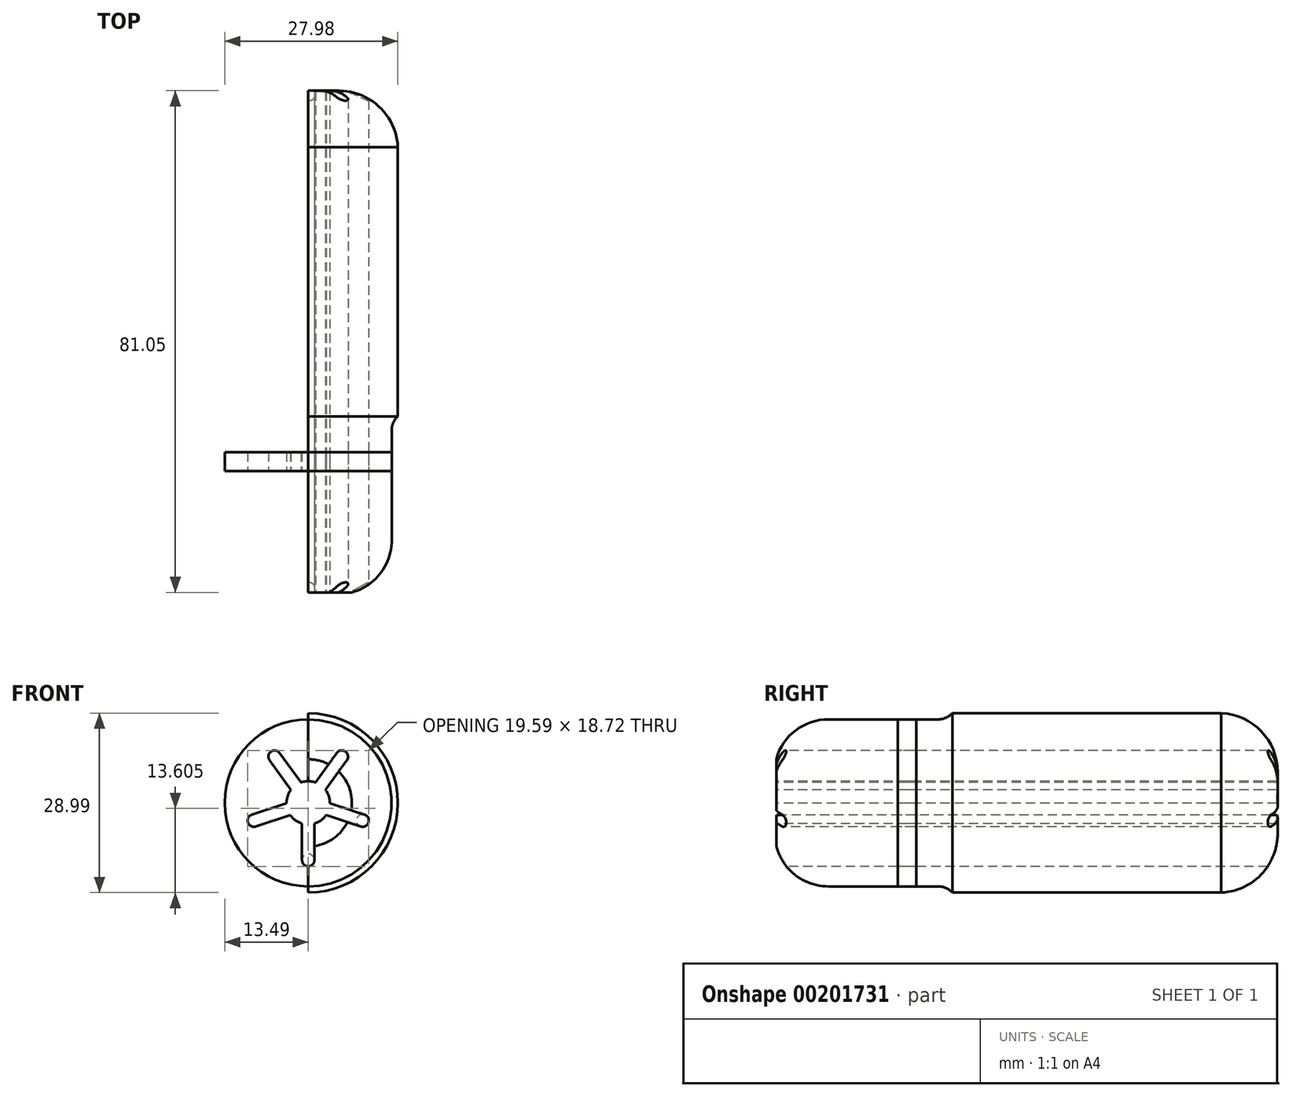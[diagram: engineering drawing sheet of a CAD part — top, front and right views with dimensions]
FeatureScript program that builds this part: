
annotation { "Feature Type Name" : "Feature", "Feature Type Description" : "" }
export const myFeature = defineFeature(function(context is Context, id is Id, definition is map)
    precondition{}
    {
        {
            var Q0;
            Q0=qCreatedBy(makeId("Right.planeOp"),FACE);
            var sketch = newSketch(context, id + "F0", { "sketchPlane" : qUnion([Q0])});
            skLineSegment(sketch, "E0.bottom", {"start": v(-3.13, 33.38) * mm, "end": v(86.87, 33.38) * mm});
            skLineSegment(sketch, "E0.top", {"start": v(-3.13, 32.38) * mm, "end": v(4.08, 32.38) * mm});
            skLineSegment(sketch, "E0.left", {"start": v(-3.13, 33.38) * mm, "end": v(-3.13, 32.38) * mm});
            skLineSegment(sketch, "E0.right", {"start": v(86.87, 33.38) * mm, "end": v(86.87, 32.38) * mm});
            skPoint(sketch, "E0.middle", {"position": v(41.87, 32.88) * mm});
            skLineSegment(sketch, "E1.bottom", {"start": v(86.87, 32.38) * mm, "end": v(81.87, 32.38) * mm, "construction": true});
            skLineSegment(sketch, "E1.top", {"start": v(86.87, 21.38) * mm, "end": v(85.87, 21.38) * mm});
            skLineSegment(sketch, "E1.left", {"start": v(86.87, 32.38) * mm, "end": v(86.87, 21.38) * mm, "construction": true});
            skLineSegment(sketch, "E1.right", {"start": v(81.87, 32.38) * mm, "end": v(81.87, 21.38) * mm, "construction": true});
            skLineSegment(sketch, "E2.bottom", {"start": v(81.87, 32.38) * mm, "end": v(71.87, 32.38) * mm, "construction": true});
            skLineSegment(sketch, "E2.top", {"start": v(81.87, 21.38) * mm, "end": v(71.87, 21.38) * mm, "construction": true});
            skLineSegment(sketch, "E2.right", {"start": v(71.87, 33.38) * mm, "end": v(71.87, 21.38) * mm, "construction": true});
            skLineSegment(sketch, "E3.0", {"start": v(85.87, 22.38) * mm, "end": v(85.37, 22.38) * mm, "construction": true});
            skLineSegment(sketch, "E4.0", {"start": v(85.87, 32.38) * mm, "end": v(85.87, 21.38) * mm, "construction": true});
            skArc(sketch, "E5", {"start": v(82.3, 22.38) * mm, "mid": v(80.84, 28.3) * mm, "end": v(76.33, 32.38) * mm});
            skArc(sketch, "E6", {"start": v(81.87, 21.38) * mm, "mid": v(79.3, 29.1) * mm, "end": v(71.87, 32.38) * mm});
            skLineSegment(sketch, "E7.trimOffspring", {"start": v(76.33, 32.38) * mm, "end": v(86.87, 32.38) * mm});
            skLineSegment(sketch, "E8.top", {"start": v(86.87, 25.38) * mm, "end": v(85.87, 25.38) * mm});
            skLineSegment(sketch, "E8.left", {"start": v(86.87, 23.38) * mm, "end": v(86.87, 25.38) * mm});
            skLineSegment(sketch, "E8.right", {"start": v(85.87, 22.38) * mm, "end": v(85.87, 22.72) * mm, "construction": true});
            skLineSegment(sketch, "E9.bottom", {"start": v(-3.13, 32.38) * mm, "end": v(-2.13, 32.38) * mm, "construction": true});
            skLineSegment(sketch, "E9.top", {"start": v(-3.13, 21.38) * mm, "end": v(-2.13, 21.38) * mm});
            skLineSegment(sketch, "E9.left", {"start": v(-3.13, 32.38) * mm, "end": v(-3.13, 21.38) * mm, "construction": true});
            skLineSegment(sketch, "E9.right", {"start": v(-2.13, 32.38) * mm, "end": v(-2.13, 21.38) * mm, "construction": true});
            skLineSegment(sketch, "E10.bottom", {"start": v(-2.13, 32.38) * mm, "end": v(4.08, 32.38) * mm, "construction": true});
            skLineSegment(sketch, "E10.top", {"start": v(-2.13, 33.38) * mm, "end": v(8.87, 33.38) * mm, "construction": true});
            skLineSegment(sketch, "E10.left", {"start": v(-2.13, 32.38) * mm, "end": v(-2.13, 33.38) * mm, "construction": true});
            skLineSegment(sketch, "E10.right", {"start": v(8.87, 32.38) * mm, "end": v(8.87, 33.38) * mm, "construction": true});
            skArc(sketch, "E11", {"start": v(4.08, 32.38) * mm, "mid": v(-1.17, 27.96) * mm, "end": v(-3.13, 21.38) * mm});
            skArc(sketch, "E12", {"start": v(8.87, 32.38) * mm, "mid": v(1.1, 29.16) * mm, "end": v(-2.13, 21.38) * mm});
            skLineSegment(sketch, "E13.trimOffspring", {"start": v(8.87, 32.38) * mm, "end": v(71.87, 32.38) * mm});
            skLineSegment(sketch, "E14", {"start": v(8.87, 21.38) * mm, "end": v(71.87, 21.38) * mm, "construction": true});
            skLineSegment(sketch, "E15.0", {"start": v(8.87, 17.38) * mm, "end": v(71.87, 17.38) * mm, "construction": true});
            skLineSegment(sketch, "E16.0", {"start": v(86.87, 23.38) * mm, "end": v(85.87, 23.38) * mm, "construction": true});
            skLineSegment(sketch, "E17.0", {"start": v(83.87, 21.38) * mm, "end": v(83.87, 25.38) * mm, "construction": true});
            skLineSegment(sketch, "E18", {"start": v(86.87, 23.38) * mm, "end": v(83.87, 21.38) * mm});
            skLineSegment(sketch, "E19.0", {"start": v(85.87, 23.92) * mm, "end": v(83.57, 22.38) * mm});
            skLineSegment(sketch, "E20.trimOffspring", {"start": v(83.87, 21.38) * mm, "end": v(81.87, 21.38) * mm});
            skLineSegment(sketch, "E21.trimOffspring", {"start": v(83.57, 22.38) * mm, "end": v(82.3, 22.38) * mm});
            skLineSegment(sketch, "E22.trimOffspring", {"start": v(85.87, 23.92) * mm, "end": v(85.87, 25.38) * mm});
            skLineSegment(sketch, "E23.bottom", {"start": v(8.87, 17.38) * mm, "end": v(-3.13, 17.38) * mm, "construction": true});
            skLineSegment(sketch, "E23.top", {"start": v(8.87, 21.38) * mm, "end": v(-3.13, 21.38) * mm, "construction": true});
            skLineSegment(sketch, "E23.left", {"start": v(8.87, 17.38) * mm, "end": v(8.87, 21.38) * mm, "construction": true});
            skLineSegment(sketch, "E23.right", {"start": v(-3.13, 17.38) * mm, "end": v(-3.13, 21.38) * mm, "construction": true});
            skSolve(sketch);
        }
        {
            var Q0;
            Q0=qCreatedBy(makeId("Right.planeOp"),FACE);
            var sketch = newSketch(context, id + "F1", { "sketchPlane" : qUnion([Q0])});
            skLineSegment(sketch, "E24.bottom", {"start": v(-3.13, 33.38) * mm, "end": v(28.58, 33.38) * mm, "construction": true});
            skLineSegment(sketch, "E24.left", {"start": v(-3.13, 33.38) * mm, "end": v(-3.13, 23.38) * mm, "construction": true});
            skLineSegment(sketch, "E24.right", {"start": v(28.58, 33.38) * mm, "end": v(28.58, 33.38) * mm});
            skLineSegment(sketch, "E25", {"start": v(28.58, 32.38) * mm, "end": v(8.84, 32.38) * mm, "construction": true});
            skArc(sketch, "E26", {"start": v(8.84, 32.38) * mm, "mid": v(1.84, 29.83) * mm, "end": v(-1.88, 23.38) * mm, "construction": true});
            skLineSegment(sketch, "E27.0", {"start": v(27.9, 31.88) * mm, "end": v(8.84, 31.88) * mm});
            skArc(sketch, "E28.0", {"start": v(8.84, 31.88) * mm, "mid": v(2.16, 29.45) * mm, "end": v(-1.38, 23.3) * mm});
            skLineSegment(sketch, "E29.0", {"start": v(26.58, 31.38) * mm, "end": v(8.84, 31.38) * mm});
            skArc(sketch, "E30.0", {"start": v(8.84, 30.88) * mm, "mid": v(2.9, 28.77) * mm, "end": v(-0.35, 23.38) * mm, "construction": true});
            skPoint(sketch, "E31.newPointB", {"position": v(28.58, 23.38) * mm});
            skArc(sketch, "E31.filletArc", {"start": v(26.58, 31.38) * mm, "mid": v(27.3, 31.5) * mm, "end": v(27.9, 31.88) * mm});
            skArc(sketch, "E32", {"start": v(8.84, 31.38) * mm, "mid": v(2.64, 29.01) * mm, "end": v(-0.4, 23.12) * mm});
            skLineSegment(sketch, "E33.trimOffspring", {"start": v(-1.37, 23.38) * mm, "end": v(-0.35, 23.38) * mm});
            skSolve(sketch);
        }
        {
            var Q0;
            Q0=qCreatedBy(makeId("Right.planeOp"),FACE);
            var sketch = newSketch(context, id + "F2", { "sketchPlane" : qUnion([Q0])});
            skLineSegment(sketch, "E34", {"start": v(86.87, 23.38) * mm, "end": v(83.87, 21.38) * mm, "construction": true});
            skLineSegment(sketch, "E35", {"start": v(83.87, 21.38) * mm, "end": v(81.87, 21.38) * mm, "construction": true});
            skLineSegment(sketch, "E36.0", {"start": v(86.87, 22.78) * mm, "end": v(84.02, 20.88) * mm});
            skLineSegment(sketch, "E37.0", {"start": v(84.02, 20.88) * mm, "end": v(81.87, 20.88) * mm});
            skLineSegment(sketch, "E38", {"start": v(86.87, 22.78) * mm, "end": v(86.87, 17.38) * mm});
            skLineSegment(sketch, "E39.0", {"start": v(66.87, 20.38) * mm, "end": v(66.87, 17.38) * mm});
            skLineSegment(sketch, "E40.0", {"start": v(81.87, 20.38) * mm, "end": v(66.87, 20.38) * mm});
            skLineSegment(sketch, "E41", {"start": v(71.87, 17.38) * mm, "end": v(66.87, 17.38) * mm});
            skLineSegment(sketch, "E42", {"start": v(71.87, 17.38) * mm, "end": v(86.87, 17.38) * mm});
            skLineSegment(sketch, "E43.0", {"start": v(81.87, 20.88) * mm, "end": v(81.87, 20.38) * mm});
            skSolve(sketch);
        }
        {
            var Q0;
            Q0=qCreatedBy(makeId("Right.planeOp"),FACE);
            var sketch = newSketch(context, id + "F3", { "sketchPlane" : qUnion([Q0])});
            skArc(sketch, "E44", {"start": v(81.87, 21.38) * mm, "mid": v(79.3, 29.1) * mm, "end": v(71.87, 32.38) * mm, "construction": true});
            skArc(sketch, "E45.0", {"start": v(81.3, 20.88) * mm, "mid": v(79.25, 28.4) * mm, "end": v(72.28, 31.88) * mm});
            skLineSegment(sketch, "E46", {"start": v(81.87, 20.38) * mm, "end": v(69.18, 20.38) * mm, "construction": true});
            skLineSegment(sketch, "E47", {"start": v(28.58, 32.38) * mm, "end": v(37.05, 32.38) * mm});
            skLineSegment(sketch, "E48", {"start": v(26.58, 31.38) * mm, "end": v(22.5, 31.38) * mm});
            skArc(sketch, "E49", {"start": v(26.58, 31.38) * mm, "mid": v(27.7, 31.64) * mm, "end": v(28.58, 32.38) * mm});
            skLineSegment(sketch, "E50.0", {"start": v(28.58, 31.88) * mm, "end": v(72.28, 31.88) * mm});
            skArc(sketch, "E51.0", {"start": v(26.58, 30.88) * mm, "mid": v(27.93, 31.2) * mm, "end": v(28.98, 32.08) * mm});
            skLineSegment(sketch, "E52.0", {"start": v(26.58, 30.88) * mm, "end": v(8.74, 30.88) * mm});
            skLineSegment(sketch, "E53.0", {"start": v(81.3, 20.88) * mm, "end": v(0.37, 20.88) * mm});
            skArc(sketch, "E54", {"start": v(8.84, 31.38) * mm, "mid": v(2.74, 29.11) * mm, "end": v(-0.35, 23.38) * mm, "construction": true});
            skArc(sketch, "E55.0", {"start": v(8.83, 30.88) * mm, "mid": v(3.5, 29.1) * mm, "end": v(0.37, 24.44) * mm});
            skLineSegment(sketch, "E56", {"start": v(-2.13, 27.58) * mm, "end": v(-2.13, 15.19) * mm, "construction": true});
            skLineSegment(sketch, "E57.trimOffspring", {"start": v(0.37, 24.44) * mm, "end": v(0.37, 20.88) * mm});
            skSolve(sketch);
        }
        {
            var Q0;
            Q0=qSketchRegion(id+"F3",true);
            var Q1;
            Q1=sQuery(id+"F0.wireOp",EDGE,"E15.0");
            revolve(context, id + "F4", {"entities" : qUnion([Q0]), "axis" : qUnion([Q1]), "revolveType" : RevolveType.ONE_DIRECTION, "angle" : 180 * degree});
        }
        {
            var Q0;
            Q0=qCreatedBy(makeId("Front.planeOp"),FACE);
            var sketch = newSketch(context, id + "F5", { "sketchPlane" : qUnion([Q0])});
            skCircle(sketch, "E58", {"center": v(0, 17.38) * mm, "radius": 14.5 * mm, "construction": true});
            skCircle(sketch, "E59", {"center": v(0, 17.38) * mm, "radius": 3.5 * mm});
            skLineSegment(sketch, "E60", {"start": v(0, 17.38) * mm, "end": v(0, 4.9) * mm, "construction": true});
            skPoint(sketch, "E61", {"position": v(0, 4.9) * mm});
            skPoint(sketch, "E62", {"position": v(-16.26, 26.77) * mm});
            skLineSegment(sketch, "E63.0", {"start": v(-1, 14.03) * mm, "end": v(-1, 8.13) * mm});
            skLineSegment(sketch, "E64.0", {"start": v(1, 14.03) * mm, "end": v(1, 8.13) * mm});
            skLineSegment(sketch, "E65", {"start": v(0, 7.13) * mm, "end": v(0, 7.13) * mm});
            skPoint(sketch, "E66.visualSharp", {"position": v(-1, 7.13) * mm});
            skArc(sketch, "E66.filletArc", {"start": v(-1, 8.13) * mm, "mid": v(-0.7, 7.43) * mm, "end": v(0, 7.13) * mm});
            skPoint(sketch, "E67.visualSharp", {"position": v(1, 7.13) * mm});
            skArc(sketch, "E67.filletArc", {"start": v(0, 7.13) * mm, "mid": v(0.7, 7.43) * mm, "end": v(1, 8.13) * mm});
            skSolve(sketch);
        }
        {
            var Q0;
            {var subQ0=sQuery(id+"F5.wireOp",EDGE,"E63.0");Q0=makeQuery(id+"F5.imprint","IMPRINT",FACE,{"disambiguationData":[TD([[makeQuery(id+"F5.imprint","IMPRINT",EDGE,{"derivedFrom":subQ0}),1.0]])]});}
            extrude(context, id + "F6", {"entities" : qUnion([Q0]), "oppositeDirection" : true, "depth" : 90 * mm});
        }
        {
            var Q0;
            Q0=qCreatedBy(makeId("Right.planeOp"),FACE);
            var sketch = newSketch(context, id + "F7", { "sketchPlane" : qUnion([Q0])});
            skLineSegment(sketch, "E68", {"start": v(0, 17.38) * mm, "end": v(41.07, 17.38) * mm});
            skSolve(sketch);
        }
        {
            var Q0;
            Q0=makeQuery(id+"F6.opExtrude","SWEPT_BODY",BODY,{"disambiguationData":[OSD([sQuery(id+"F5.wireOp",EDGE,"E59"),sQuery(id+"F5.wireOp",EDGE,"E63.0"),sQuery(id+"F5.wireOp",EDGE,"E64.0"),sQuery(id+"F5.wireOp",EDGE,"c18d3147-b101-4655-83fc-4fb6f8fd4f04")])]});
            var Q1;
            Q1=sQuery(id+"F7.wireOp",EDGE,"E68");
            circularPattern(context, id + "F8", {"entities" : qUnion([Q0]), "axis" : qUnion([Q1]), "angle" : 360 * degree, "instanceCount" : 5, "equalSpace" : true});
        }
        {
            var Q0;
            Q0=makeQuery(id+"F6.opExtrude","SWEPT_BODY",BODY,{"disambiguationData":[OSD([sQuery(id+"F5.wireOp",EDGE,"E59"),sQuery(id+"F5.wireOp",EDGE,"E63.0"),sQuery(id+"F5.wireOp",EDGE,"E64.0"),sQuery(id+"F5.wireOp",EDGE,"E66.filletArc"),sQuery(id+"F5.wireOp",EDGE,"E67.filletArc")])]});
            var Q1;
            Q1=makeQuery(id+"F8.opPattern","COPY",BODY,{"derivedFrom":makeQuery(id+"F6.opExtrude","SWEPT_BODY",BODY,{"disambiguationData":[OSD([sQuery(id+"F5.wireOp",EDGE,"E59"),sQuery(id+"F5.wireOp",EDGE,"E63.0"),sQuery(id+"F5.wireOp",EDGE,"E64.0"),sQuery(id+"F5.wireOp",EDGE,"E66.filletArc"),sQuery(id+"F5.wireOp",EDGE,"E67.filletArc")])]}),"instanceName":"4"});
            var Q2;
            Q2=makeQuery(id+"F8.opPattern","COPY",BODY,{"derivedFrom":makeQuery(id+"F6.opExtrude","SWEPT_BODY",BODY,{"disambiguationData":[OSD([sQuery(id+"F5.wireOp",EDGE,"E59"),sQuery(id+"F5.wireOp",EDGE,"E63.0"),sQuery(id+"F5.wireOp",EDGE,"E64.0"),sQuery(id+"F5.wireOp",EDGE,"E66.filletArc"),sQuery(id+"F5.wireOp",EDGE,"E67.filletArc")])]}),"instanceName":"3"});
            var Q3;
            Q3=makeQuery(id+"F4.opRevolve","SWEPT_BODY",BODY,{"disambiguationData":[OSD([sQuery(id+"F3.wireOp",EDGE,"E45.0"),sQuery(id+"F3.wireOp",EDGE,"E50.0"),sQuery(id+"F3.wireOp",EDGE,"E51.0"),sQuery(id+"F3.wireOp",EDGE,"E52.0"),sQuery(id+"F3.wireOp",EDGE,"E53.0"),sQuery(id+"F3.wireOp",EDGE,"E55.0"),sQuery(id+"F3.wireOp",EDGE,"E57.trimOffspring")])]});
            booleanBodies(context, id + "F9", {"operationType" : BooleanOperationType.SUBTRACTION, "tools" : qUnion([Q0, Q1, Q2]), "targets" : qUnion([Q3]), "keepTools" : true});
        }
        {
            var Q0;
            Q0 = qSketchRegion(id + "F3", true);
            var Q1;
            Q1=sQuery(id+"F0.wireOp",EDGE,"E15.0");
            revolve(context, id + "F10", {"entities" : qUnion([Q0]), "axis" : qUnion([Q1]), "revolveType" : RevolveType.FULL});
        }
        {
            var Q0;
            Q0=qCreatedBy(makeId("Front.planeOp"),FACE);
            var sketch = newSketch(context, id + "F11", { "sketchPlane" : qUnion([Q0])});
            skCircle(sketch, "E69.0", {"center": v(0, 17.38) * mm, "radius": 13.5 * mm});
            skSolve(sketch);
        }
        {
            var Q0;
            Q0=makeQuery(id+"F11.imprint","IMPRINT",FACE,{"disambiguationData":[TD([[makeQuery(id+"F11.imprint","IMPRINT",EDGE,{"derivedFrom":sQuery(id+"F11.wireOp",EDGE,"E69.0")}),1.0]])]});
            extrude(context, id + "F12", {"entities" : qUnion([Q0]), "oppositeDirection" : true, "depth" : 23 * mm, "hasSecondDirection" : true, "secondDirectionOppositeDirection" : true, "secondDirectionDepth" : 20 * mm});
        }
        {
            var Q0;
            Q0=makeQuery(id+"F6.opExtrude","SWEPT_BODY",BODY,{"disambiguationData":[OSD([sQuery(id+"F5.wireOp",EDGE,"E59"),sQuery(id+"F5.wireOp",EDGE,"E63.0"),sQuery(id+"F5.wireOp",EDGE,"E64.0"),sQuery(id+"F5.wireOp",EDGE,"E66.filletArc"),sQuery(id+"F5.wireOp",EDGE,"E67.filletArc")])]});
            var Q1;
            Q1=makeQuery(id+"F8.opPattern","COPY",BODY,{"derivedFrom":makeQuery(id+"F6.opExtrude","SWEPT_BODY",BODY,{"disambiguationData":[OSD([sQuery(id+"F5.wireOp",EDGE,"E59"),sQuery(id+"F5.wireOp",EDGE,"E63.0"),sQuery(id+"F5.wireOp",EDGE,"E64.0"),sQuery(id+"F5.wireOp",EDGE,"E66.filletArc"),sQuery(id+"F5.wireOp",EDGE,"E67.filletArc")])]}),"instanceName":"4"});
            var Q2;
            Q2=makeQuery(id+"F8.opPattern","COPY",BODY,{"derivedFrom":makeQuery(id+"F6.opExtrude","SWEPT_BODY",BODY,{"disambiguationData":[OSD([sQuery(id+"F5.wireOp",EDGE,"E59"),sQuery(id+"F5.wireOp",EDGE,"E63.0"),sQuery(id+"F5.wireOp",EDGE,"E64.0"),sQuery(id+"F5.wireOp",EDGE,"E66.filletArc"),sQuery(id+"F5.wireOp",EDGE,"E67.filletArc")])]}),"instanceName":"3"});
            var Q3;
            Q3=makeQuery(id+"F8.opPattern","COPY",BODY,{"derivedFrom":makeQuery(id+"F6.opExtrude","SWEPT_BODY",BODY,{"disambiguationData":[OSD([sQuery(id+"F5.wireOp",EDGE,"E59"),sQuery(id+"F5.wireOp",EDGE,"E63.0"),sQuery(id+"F5.wireOp",EDGE,"E64.0"),sQuery(id+"F5.wireOp",EDGE,"E66.filletArc"),sQuery(id+"F5.wireOp",EDGE,"E67.filletArc")])]}),"instanceName":"2"});
            var Q4;
            Q4=makeQuery(id+"F8.opPattern","COPY",BODY,{"derivedFrom":makeQuery(id+"F6.opExtrude","SWEPT_BODY",BODY,{"disambiguationData":[OSD([sQuery(id+"F5.wireOp",EDGE,"E59"),sQuery(id+"F5.wireOp",EDGE,"E63.0"),sQuery(id+"F5.wireOp",EDGE,"E64.0"),sQuery(id+"F5.wireOp",EDGE,"E66.filletArc"),sQuery(id+"F5.wireOp",EDGE,"E67.filletArc")])]}),"instanceName":"1"});
            var Q5;
            Q5=makeQuery(id+"F10.opRevolve","SWEPT_BODY",BODY,{"disambiguationData":[OSD([sQuery(id+"F3.wireOp",EDGE,"E45.0"),sQuery(id+"F3.wireOp",EDGE,"E50.0"),sQuery(id+"F3.wireOp",EDGE,"E51.0"),sQuery(id+"F3.wireOp",EDGE,"E52.0"),sQuery(id+"F3.wireOp",EDGE,"E53.0"),sQuery(id+"F3.wireOp",EDGE,"E55.0"),sQuery(id+"F3.wireOp",EDGE,"E57.trimOffspring")])]});
            booleanBodies(context, id + "F13", {"operationType" : BooleanOperationType.SUBTRACTION, "tools" : qUnion([Q0, Q1, Q2, Q3, Q4]), "targets" : qUnion([Q5])});
        }
        {
            var Q0;
            Q0=makeQuery(id+"F10.opRevolve","SWEPT_BODY",BODY,{"disambiguationData":[OSD([sQuery(id+"F3.wireOp",EDGE,"E45.0"),sQuery(id+"F3.wireOp",EDGE,"E50.0"),sQuery(id+"F3.wireOp",EDGE,"E51.0"),sQuery(id+"F3.wireOp",EDGE,"E52.0"),sQuery(id+"F3.wireOp",EDGE,"E53.0"),sQuery(id+"F3.wireOp",EDGE,"E55.0"),sQuery(id+"F3.wireOp",EDGE,"E57.trimOffspring")])]});
            var Q1;
            Q1=makeQuery(id+"F12.opExtrude","SWEPT_BODY",BODY,{"disambiguationData":[OSD([sQuery(id+"F11.wireOp",EDGE,"E69.0")])]});
            booleanBodies(context, id + "F14", {"operationType" : BooleanOperationType.INTERSECTION, "tools" : qUnion([Q0, Q1])});
        }
    });
